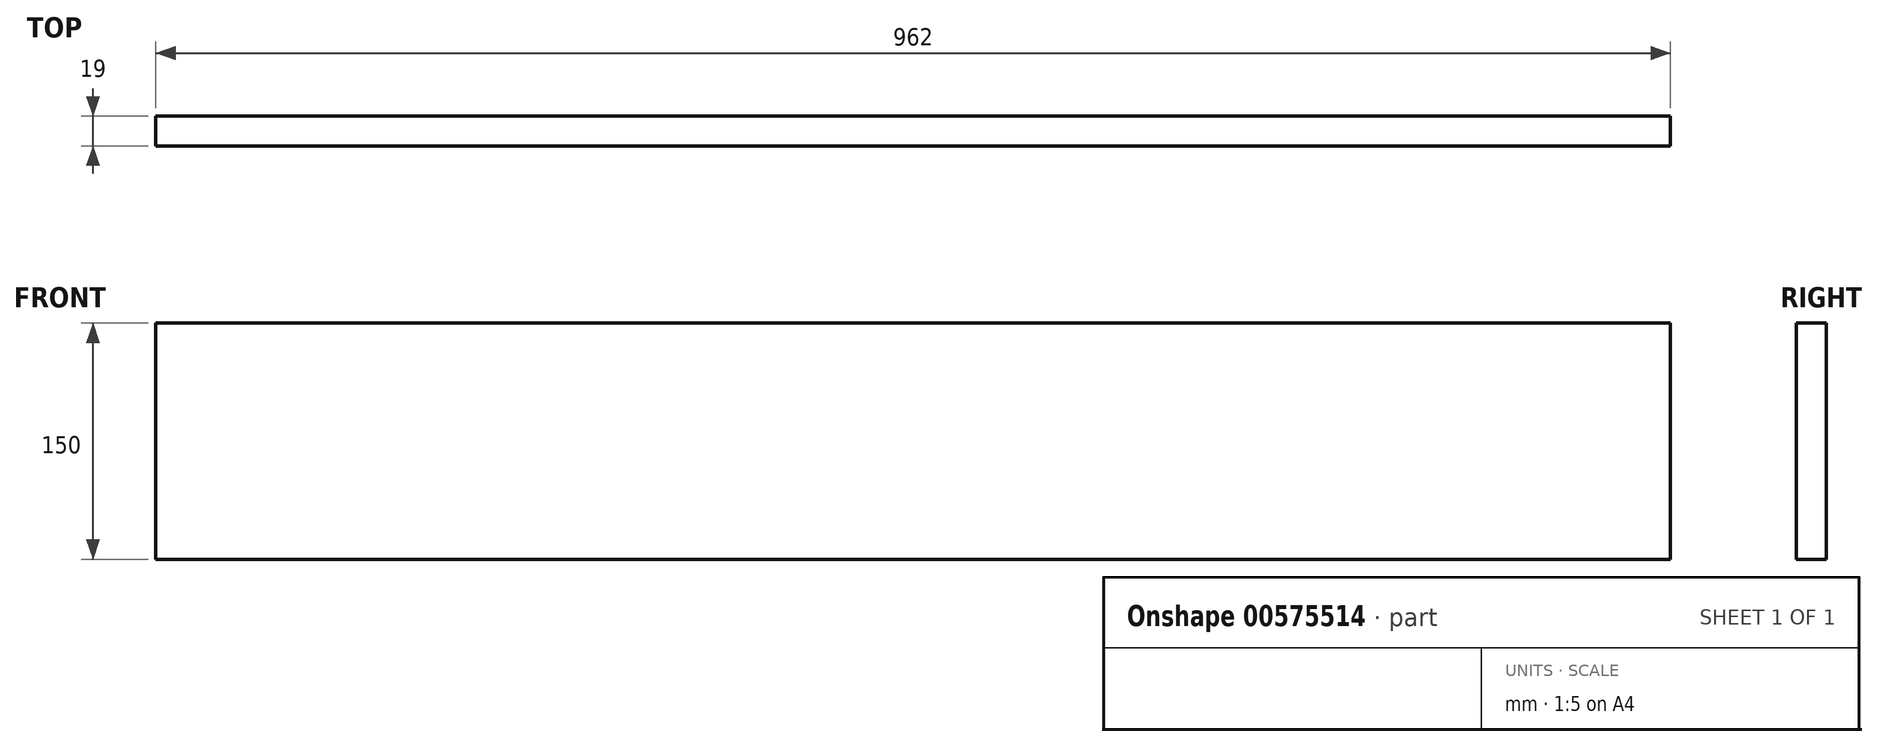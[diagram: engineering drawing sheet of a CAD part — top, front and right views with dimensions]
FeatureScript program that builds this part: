
annotation { "Feature Type Name" : "Feature", "Feature Type Description" : "" }
export const myFeature = defineFeature(function(context is Context, id is Id, definition is map)
    precondition{}
    {
        {
            var Q0;
            Q0=qCreatedBy(makeId("Top.planeOp"),FACE);
            var sketch = newSketch(context, id + "F0", { "sketchPlane" : qUnion([Q0])});
            skPoint(sketch, "E0.middle", {"position": v(0, 0) * mm});
            skLineSegment(sketch, "E1.bottom", {"start": v(500, 170) * mm, "end": v(-500, 170) * mm});
            skLineSegment(sketch, "E1.top", {"start": v(500, -170) * mm, "end": v(-500, -170) * mm});
            skLineSegment(sketch, "E1.left", {"start": v(500, 170) * mm, "end": v(500, -170) * mm});
            skLineSegment(sketch, "E1.right", {"start": v(-500, 170) * mm, "end": v(-500, -170) * mm});
            skLineSegment(sketch, "E2.bottom", {"start": v(-481, 151) * mm, "end": v(481, 151) * mm});
            skLineSegment(sketch, "E2.top", {"start": v(-481, -151) * mm, "end": v(481, -151) * mm});
            skLineSegment(sketch, "E2.left", {"start": v(-481, 151) * mm, "end": v(-481, -151) * mm});
            skLineSegment(sketch, "E2.right", {"start": v(481, 151) * mm, "end": v(481, -151) * mm});
            skLineSegment(sketch, "E3.bottom", {"start": v(481, 9.5) * mm, "end": v(-481, 9.5) * mm});
            skLineSegment(sketch, "E3.top", {"start": v(481, -9.5) * mm, "end": v(-481, -9.5) * mm});
            skLineSegment(sketch, "E3.left", {"start": v(481, 9.5) * mm, "end": v(481, -9.5) * mm});
            skLineSegment(sketch, "E3.right", {"start": v(-481, 9.5) * mm, "end": v(-481, -9.5) * mm});
            skSolve(sketch);
        }
        {
            var Q0;
            {var subQ2=sQuery(id+"F0.wireOp",EDGE,"E3.bottom");Q0=makeQuery(id+"F0.imprint","IMPRINT",FACE,{"disambiguationData":[TD([[makeQuery(id+"F0.imprint","IMPRINT",EDGE,{"derivedFrom":subQ2}),1.0]])]});}
            extrude(context, id + "F1", {"entities" : qUnion([Q0]), "depth" : 150 * mm, "offsetDistance" : 25 * mm});
        }
    });
